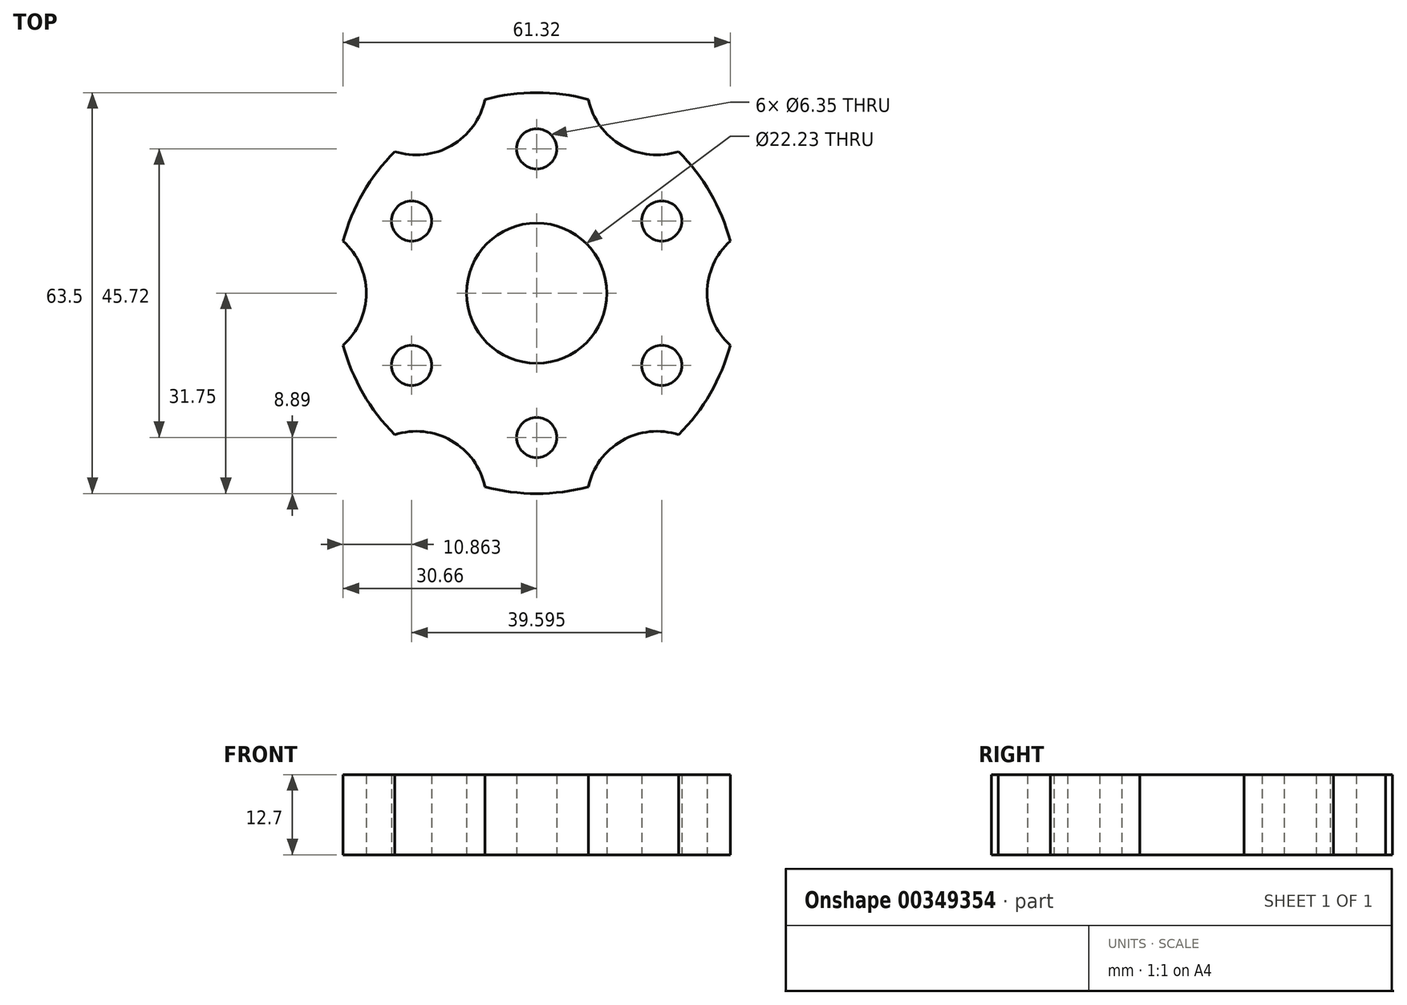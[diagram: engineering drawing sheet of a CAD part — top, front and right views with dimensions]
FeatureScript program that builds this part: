
annotation { "Feature Type Name" : "Feature", "Feature Type Description" : "" }
export const myFeature = defineFeature(function(context is Context, id is Id, definition is map)
    precondition{}
    {
        {
            var Q0;
            Q0=qCreatedBy(makeId("Top.planeOp"),FACE);
            var sketch = newSketch(context, id + "F0", { "sketchPlane" : qUnion([Q0])});
            skCircle(sketch, "E0", {"center": v(0, 0) * mm, "radius": 31.75 * mm});
            skCircle(sketch, "E1", {"center": v(0, 0) * mm, "radius": 11.11 * mm});
            skSolve(sketch);
        }
        {
            var Q0;
            Q0=makeQuery(id+"F0.imprint","IMPRINT",FACE,{"disambiguationData":[TD([[makeQuery(id+"F0.imprint","IMPRINT",EDGE,{"derivedFrom":sQuery(id+"F0.wireOp",EDGE,"E0")}),1.0]])]});
            extrude(context, id + "F1", {"entities" : qUnion([Q0]), "depth" : 12.7 * mm});
        }
        {
            var Q0;
            Q0=qCreatedBy(makeId("Top.planeOp"),FACE);
            var sketch = newSketch(context, id + "F2", { "sketchPlane" : qUnion([Q0])});
            skCircle(sketch, "E2", {"center": v(0, 0) * mm, "radius": 38.1 * mm});
            skCircle(sketch, "E3", {"center": v(-38.1, 0) * mm, "radius": 11.11 * mm});
            skCircle(sketch, "E4.1.0", {"center": v(-19.05, -33) * mm, "radius": 11.11 * mm});
            skCircle(sketch, "E4.2.0", {"center": v(19.05, -33) * mm, "radius": 11.11 * mm});
            skCircle(sketch, "E4.3.0", {"center": v(38.1, 0) * mm, "radius": 11.11 * mm});
            skCircle(sketch, "E4.4.0", {"center": v(19.05, 33) * mm, "radius": 11.11 * mm});
            skCircle(sketch, "E4.5.0", {"center": v(-19.05, 33) * mm, "radius": 11.11 * mm});
            skSolve(sketch);
        }
        {
            var Q0;
            {var subQ0=sQuery(id+"F2.wireOp",EDGE,"E4.2.0");var subQ1=sQuery(id+"F2.wireOp",EDGE,"E2");var subQ2=makeQuery(id+"F2.imprint","INTERSECT",VERTEX,{"disambiguationData":[OD(0.0)],"derivedFrom":[subQ1,subQ0]});Q0=makeQuery(id+"F2.imprint","IMPRINT",FACE,{"disambiguationData":[TD([[makeQuery(id+"F2.imprint","IMPRINT",EDGE,{"disambiguationData":[TD([[subQ2,-1.0]])],"derivedFrom":subQ1}),1.0]])]});}
            var Q1;
            {var subQ0=sQuery(id+"F2.wireOp",EDGE,"E4.1.0");var subQ1=sQuery(id+"F2.wireOp",EDGE,"E2");var subQ2=makeQuery(id+"F2.imprint","INTERSECT",VERTEX,{"disambiguationData":[OD(0.0)],"derivedFrom":[subQ1,subQ0]});Q1=makeQuery(id+"F2.imprint","IMPRINT",FACE,{"disambiguationData":[TD([[makeQuery(id+"F2.imprint","IMPRINT",EDGE,{"disambiguationData":[TD([[subQ2,-1.0]])],"derivedFrom":subQ1}),1.0]])]});}
            var Q2;
            {var subQ0=sQuery(id+"F2.wireOp",EDGE,"E3");var subQ1=sQuery(id+"F2.wireOp",EDGE,"E2");var subQ2=makeQuery(id+"F2.imprint","INTERSECT",VERTEX,{"disambiguationData":[OD(0.0)],"derivedFrom":[subQ1,subQ0]});Q2=makeQuery(id+"F2.imprint","IMPRINT",FACE,{"disambiguationData":[TD([[makeQuery(id+"F2.imprint","IMPRINT",EDGE,{"disambiguationData":[TD([[subQ2,-1.0]])],"derivedFrom":subQ1}),1.0]])]});}
            var Q3;
            {var subQ0=sQuery(id+"F2.wireOp",EDGE,"E4.5.0");var subQ1=sQuery(id+"F2.wireOp",EDGE,"E2");var subQ2=makeQuery(id+"F2.imprint","INTERSECT",VERTEX,{"disambiguationData":[OD(0.0)],"derivedFrom":[subQ1,subQ0]});Q3=makeQuery(id+"F2.imprint","IMPRINT",FACE,{"disambiguationData":[TD([[makeQuery(id+"F2.imprint","IMPRINT",EDGE,{"disambiguationData":[TD([[subQ2,-1.0]])],"derivedFrom":subQ1}),1.0]])]});}
            var Q4;
            {var subQ0=sQuery(id+"F2.wireOp",EDGE,"E4.4.0");var subQ1=sQuery(id+"F2.wireOp",EDGE,"E2");var subQ2=makeQuery(id+"F2.imprint","INTERSECT",VERTEX,{"disambiguationData":[OD(0.0)],"derivedFrom":[subQ1,subQ0]});Q4=makeQuery(id+"F2.imprint","IMPRINT",FACE,{"disambiguationData":[TD([[makeQuery(id+"F2.imprint","IMPRINT",EDGE,{"disambiguationData":[TD([[subQ2,-1.0]])],"derivedFrom":subQ1}),1.0]])]});}
            var Q5;
            {var subQ0=sQuery(id+"F2.wireOp",EDGE,"E4.3.0");var subQ1=sQuery(id+"F2.wireOp",EDGE,"E2");var subQ2=makeQuery(id+"F2.imprint","INTERSECT",VERTEX,{"disambiguationData":[OD(0.0)],"derivedFrom":[subQ1,subQ0]});Q5=makeQuery(id+"F2.imprint","IMPRINT",FACE,{"disambiguationData":[TD([[makeQuery(id+"F2.imprint","IMPRINT",EDGE,{"disambiguationData":[TD([[subQ2,1.0]])],"derivedFrom":subQ1}),1.0]])]});}
            extrude(context, id + "F3", {"entities" : qUnion([Q0, Q1, Q2, Q3, Q4, Q5]), "operationType" : NewBodyOperationType.REMOVE, "depth" : 25.4 * mm});
        }
        {
            var Q0;
            Q0=qCreatedBy(makeId("Top.planeOp"),FACE);
            var sketch = newSketch(context, id + "F4", { "sketchPlane" : qUnion([Q0])});
            skCircle(sketch, "E5", {"center": v(0, 22.86) * mm, "radius": 3.18 * mm});
            skCircle(sketch, "E6.1.0", {"center": v(-19.8, 11.43) * mm, "radius": 3.18 * mm});
            skCircle(sketch, "E6.2.0", {"center": v(-19.8, -11.43) * mm, "radius": 3.18 * mm});
            skCircle(sketch, "E6.3.0", {"center": v(0, -22.86) * mm, "radius": 3.18 * mm});
            skCircle(sketch, "E6.4.0", {"center": v(19.8, -11.43) * mm, "radius": 3.18 * mm});
            skCircle(sketch, "E6.5.0", {"center": v(19.8, 11.43) * mm, "radius": 3.18 * mm});
            skPoint(sketch, "E6.center", {"position": v(0, 0) * mm});
            skSolve(sketch);
        }
        {
            var Q0;
            Q0=qSketchRegion(id+"F4",true);
            extrude(context, id + "F5", {"entities" : qUnion([Q0]), "operationType" : NewBodyOperationType.REMOVE, "depth" : 25.4 * mm});
        }
    });
